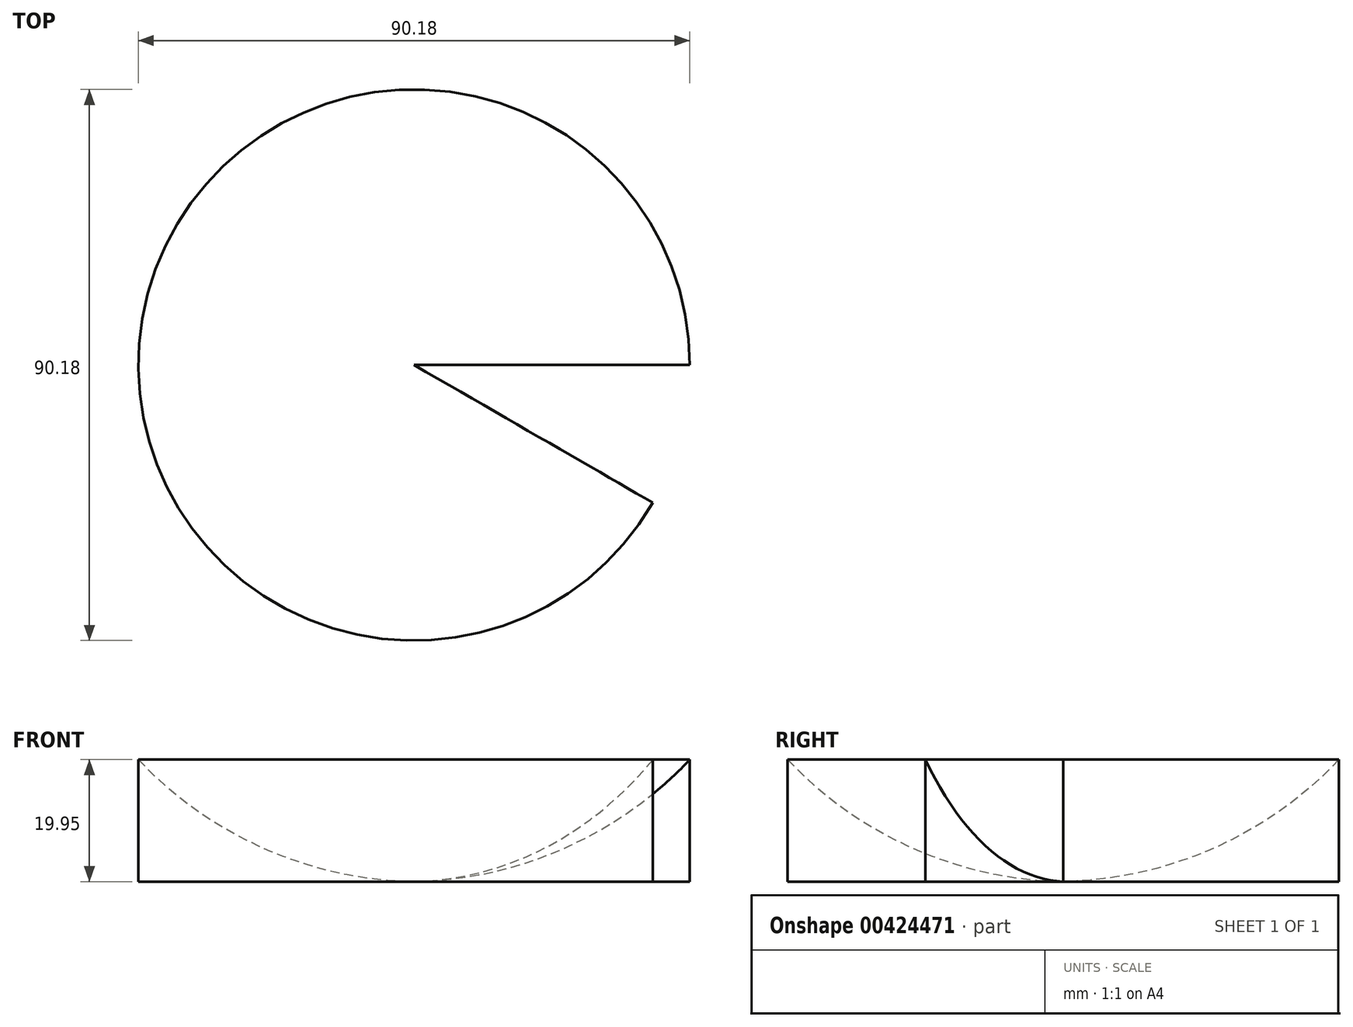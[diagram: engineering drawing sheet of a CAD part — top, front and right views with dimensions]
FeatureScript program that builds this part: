
annotation { "Feature Type Name" : "Feature", "Feature Type Description" : "" }
export const myFeature = defineFeature(function(context is Context, id is Id, definition is map)
    precondition{}
    {
        {
            var Q0;
            Q0=qCreatedBy(makeId("Front.planeOp"),FACE);
            var sketch = newSketch(context, id + "F0", { "sketchPlane" : qUnion([Q0])});
            skArc(sketch, "E0", {"start": v(0, 0) * mm, "mid": v(24.55, 5.44) * mm, "end": v(45.1, 19.95) * mm});
            skLineSegment(sketch, "E1", {"start": v(45.1, 19.95) * mm, "end": v(45.1, 0) * mm});
            skLineSegment(sketch, "E2", {"start": v(45.1, 0) * mm, "end": v(0, 0) * mm});
            skLineSegment(sketch, "E3", {"start": v(0, 0) * mm, "end": v(0, 21.4) * mm});
            skSolve(sketch);
        }
        {
            var Q0;
            Q0 = qSketchRegion(id + "F0", true);
            var Q1;
            Q1=sQuery(id+"F0.wireOp",EDGE,"E3");
            revolve(context, id + "F1", {"entities" : qUnion([Q0]), "axis" : qUnion([Q1]), "revolveType" : RevolveType.ONE_DIRECTION, "angle" : 330 * degree});
        }
    });
